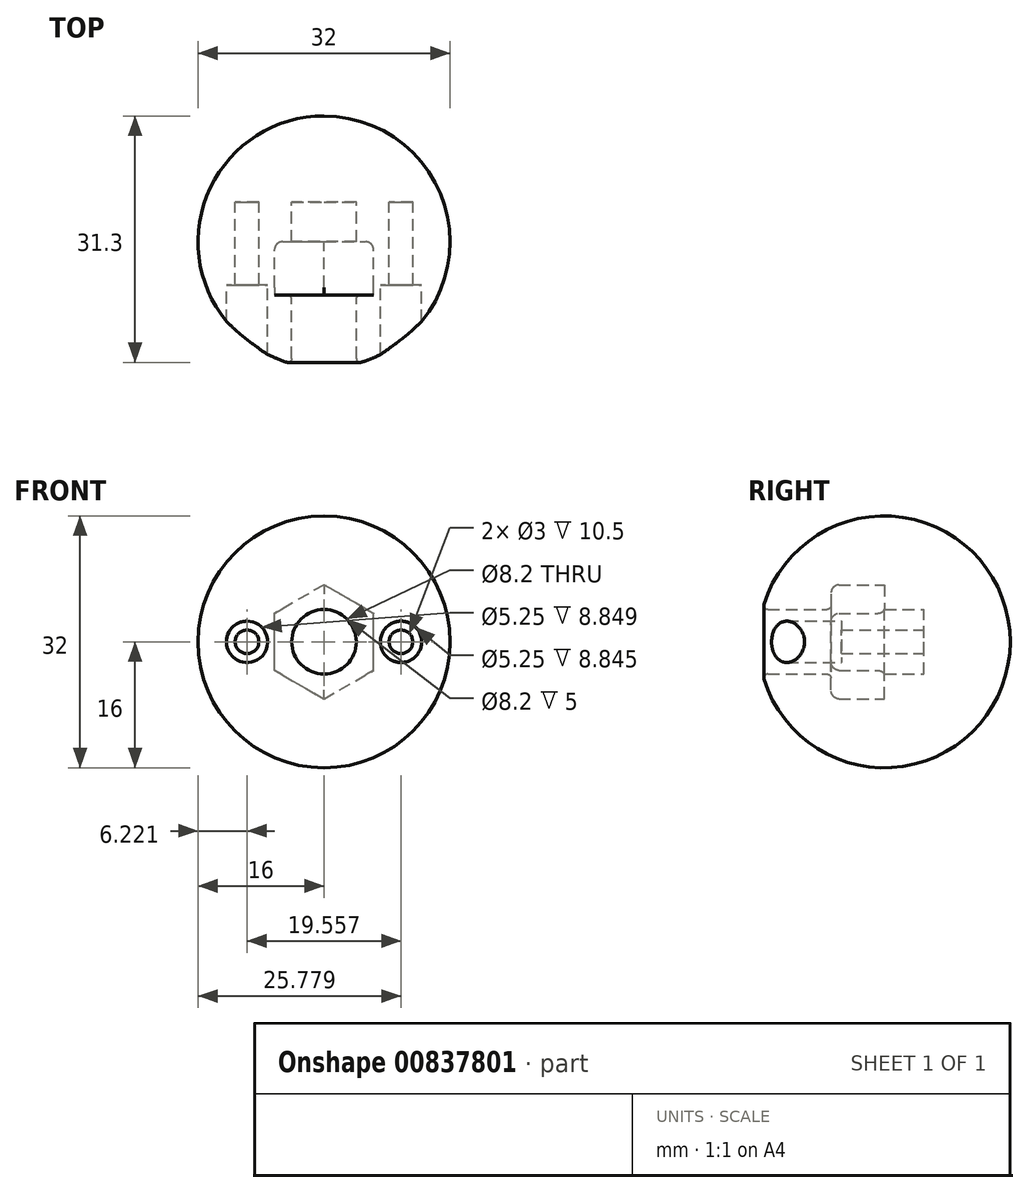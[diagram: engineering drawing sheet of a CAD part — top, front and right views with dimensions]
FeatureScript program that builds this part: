
annotation { "Feature Type Name" : "Feature", "Feature Type Description" : "" }
export const myFeature = defineFeature(function(context is Context, id is Id, definition is map)
    precondition{}
    {
        {
            var Q0;
            Q0=qCreatedBy(makeId("Top.planeOp"),FACE);
            var sketch = newSketch(context, id + "F0", { "sketchPlane" : qUnion([Q0])});
            skArc(sketch, "E0", {"start": v(4.1, -15.47) * mm, "mid": v(0, 16) * mm, "end": v(-4.1, -15.47) * mm});
            skLineSegment(sketch, "E1", {"start": v(0, -15.47) * mm, "end": v(0, 16) * mm});
            skLineSegment(sketch, "E2", {"start": v(0, -12.17) * mm, "end": v(4.1, -12.17) * mm, "construction": true});
            skLineSegment(sketch, "E3", {"start": v(4.1, -12.17) * mm, "end": v(4.1, -15.47) * mm, "construction": true});
            skLineSegment(sketch, "E4", {"start": v(4.1, -15.47) * mm, "end": v(-4.1, -15.47) * mm});
            skPoint(sketch, "E5.orphan", {"position": v(0, -16) * mm});
            skSolve(sketch);
        }
        {
            var Q0;
            {var subQ3=sQuery(id+"F0.wireOp",EDGE,"E1");Q0=makeQuery(id+"F0.imprint","IMPRINT",FACE,{"disambiguationData":[TD([[makeQuery(id+"F0.imprint","IMPRINT",EDGE,{"derivedFrom":subQ3}),-1.0]])]});}
            var Q1;
            Q1=sQuery(id+"F0.wireOp",EDGE,"E1");
            revolve(context, id + "F1", {"surfaceOperationType" : NewSurfaceOperationType.NEW, "entities" : qUnion([Q0]), "axis" : qUnion([Q1]), "revolveType" : RevolveType.FULL});
        }
        {
            var Q0;
            Q0=makeQuery(id+"F1.opRevolve","SWEPT_FACE",FACE,{"disambiguationData":[OSD([sQuery(id+"F0.wireOp",EDGE,"E4")])]});
            extrude(context, id + "F2", {"entities" : qUnion([Q0]), "operationType" : NewBodyOperationType.REMOVE, "oppositeDirection" : true, "depth" : 20.5 * mm, "offsetDistance" : 25 * mm});
        }
        {
            var Q0;
            Q0=makeQuery(id+"F2.boolean.opBoolean","COPY",FACE,{"derivedFrom":makeQuery(id+"F2.opExtrude","CAP_FACE",FACE,{"disambiguationData":[OSD([sQuery(id+"F0.wireOp",EDGE,"E4")])],"isStart":false})});
            var sketch = newSketch(context, id + "F3", { "sketchPlane" : qUnion([Q0])});
            skLineSegment(sketch, "E6", {"start": v(0, 0) * mm, "end": v(-12, 0) * mm, "construction": true});
            skLineSegment(sketch, "E7", {"start": v(0, 0) * mm, "end": v(12, 0) * mm, "construction": true});
            skLineSegment(sketch, "E8", {"start": v(0, 0) * mm, "end": v(0, 7.25) * mm, "construction": true});
            skLineSegment(sketch, "E9", {"start": v(0, 0) * mm, "end": v(0, -7.25) * mm, "construction": true});
            skLineSegment(sketch, "E10", {"start": v(0, 0) * mm, "end": v(3.55, 2.05) * mm, "construction": true});
            skLineSegment(sketch, "E11", {"start": v(0, 0) * mm, "end": v(3.55, -2.05) * mm, "construction": true});
            skLineSegment(sketch, "E12", {"start": v(0, 0) * mm, "end": v(-3.55, -2.05) * mm, "construction": true});
            skLineSegment(sketch, "E13", {"start": v(0, 0) * mm, "end": v(-3.55, 2.05) * mm, "construction": true});
            skLineSegment(sketch, "E14", {"start": v(3.55, 2.05) * mm, "end": v(6.28, 3.63) * mm, "construction": true});
            skLineSegment(sketch, "E15", {"start": v(-3.55, 2.05) * mm, "end": v(-6.28, 3.63) * mm, "construction": true});
            skLineSegment(sketch, "E16", {"start": v(-3.55, -2.05) * mm, "end": v(-6.28, -3.63) * mm, "construction": true});
            skLineSegment(sketch, "E17", {"start": v(3.55, -2.05) * mm, "end": v(6.28, -3.62) * mm, "construction": true});
            skLineSegment(sketch, "E18", {"start": v(0, 7.25) * mm, "end": v(-6.28, 3.62) * mm});
            skLineSegment(sketch, "E19", {"start": v(-6.28, 3.62) * mm, "end": v(-6.28, -3.63) * mm});
            skLineSegment(sketch, "E20", {"start": v(-6.28, -3.63) * mm, "end": v(0, -7.25) * mm});
            skLineSegment(sketch, "E21", {"start": v(0, -7.25) * mm, "end": v(6.28, -3.62) * mm});
            skLineSegment(sketch, "E22", {"start": v(6.28, -3.62) * mm, "end": v(6.28, 3.63) * mm});
            skLineSegment(sketch, "E23", {"start": v(6.28, 3.63) * mm, "end": v(0, 7.25) * mm});
            skLineSegment(sketch, "E24", {"start": v(-6.28, 3.63) * mm, "end": v(-13.28, 3.62) * mm});
            skLineSegment(sketch, "E25", {"start": v(-13.28, 3.62) * mm, "end": v(-13.28, -3.63) * mm});
            skLineSegment(sketch, "E26", {"start": v(-13.28, -3.63) * mm, "end": v(-6.28, -3.63) * mm});
            skLineSegment(sketch, "E27", {"start": v(6.28, 3.63) * mm, "end": v(13.28, 3.63) * mm});
            skLineSegment(sketch, "E28", {"start": v(13.28, 3.63) * mm, "end": v(13.28, -3.62) * mm});
            skLineSegment(sketch, "E29", {"start": v(13.28, -3.62) * mm, "end": v(6.28, -3.62) * mm});
            skCircle(sketch, "E30", {"center": v(-9.78, 0) * mm, "radius": 1.5 * mm});
            skPoint(sketch, "E30.centerSnap0", {"position": v(-9.78, 3.62) * mm});
            skCircle(sketch, "E31", {"center": v(9.78, 0) * mm, "radius": 1.5 * mm});
            skPoint(sketch, "E31.centerSnap0", {"position": v(9.78, 3.63) * mm});
            skSolve(sketch);
        }
        {
            var Q0;
            Q0 = qSketchRegion(id + "F3", true);
            extrude(context, id + "F4", {"entities" : qUnion([Q0]), "operationType" : NewBodyOperationType.ADD, "depth" : 25 * mm, "offsetDistance" : 25 * mm});
        }
        {
            var Q0;
            Q0=makeQuery(id+"F4.opExtrude","CAP_FACE",FACE,{"disambiguationData":[OSD([sQuery(id+"F3.wireOp",EDGE,"E18"),sQuery(id+"F3.wireOp",EDGE,"E20"),sQuery(id+"F3.wireOp",EDGE,"E21"),sQuery(id+"F3.wireOp",EDGE,"E23"),sQuery(id+"F3.wireOp",EDGE,"E24"),sQuery(id+"F3.wireOp",EDGE,"E25"),sQuery(id+"F3.wireOp",EDGE,"E26"),sQuery(id+"F3.wireOp",EDGE,"E27"),sQuery(id+"F3.wireOp",EDGE,"E28"),sQuery(id+"F3.wireOp",EDGE,"E29"),sQuery(id+"F3.wireOp",EDGE,"E30"),sQuery(id+"F3.wireOp",EDGE,"E31")])],"isStart":false});
            var sketch = newSketch(context, id + "F5", { "sketchPlane" : qUnion([Q0])});
            skCircle(sketch, "E32", {"center": v(-9.78, 0) * mm, "radius": 1.5 * mm});
            skCircle(sketch, "E33", {"center": v(9.78, 0) * mm, "radius": 1.5 * mm});
            skSolve(sketch);
        }
        {
            var Q0;
            Q0=makeQuery(id+"F5.imprint","IMPRINT",FACE,{"disambiguationData":[TD([[makeQuery(id+"F5.imprint","IMPRINT",EDGE,{"derivedFrom":sQuery(id+"F5.wireOp",EDGE,"E32")}),-1.0]])]});
            var Q1;
            Q1=makeQuery(id+"F5.imprint","IMPRINT",FACE,{"disambiguationData":[TD([[makeQuery(id+"F5.imprint","IMPRINT",EDGE,{"derivedFrom":sQuery(id+"F5.wireOp",EDGE,"E32")}),1.0]])]});
            var Q2;
            Q2=makeQuery(id+"F5.imprint","IMPRINT",FACE,{"disambiguationData":[TD([[makeQuery(id+"F5.imprint","IMPRINT",EDGE,{"derivedFrom":sQuery(id+"F5.wireOp",EDGE,"E33")}),1.0]])]});
            extrude(context, id + "F6", {"entities" : qUnion([Q0, Q1, Q2]), "operationType" : NewBodyOperationType.REMOVE, "oppositeDirection" : true, "depth" : 25 * mm, "offsetDistance" : 25 * mm});
        }
        {
            var Q0;
            Q0=makeQuery(id+"F3.imprint","IMPRINT",FACE,{"disambiguationData":[TD([[makeQuery(id+"F3.imprint","IMPRINT",EDGE,{"derivedFrom":sQuery(id+"F3.wireOp",EDGE,"E18")}),1.0]])]});
            var Q1;
            Q1=makeQuery(id+"F3.imprint","IMPRINT",FACE,{"disambiguationData":[TD([[makeQuery(id+"F3.imprint","IMPRINT",EDGE,{"derivedFrom":sQuery(id+"F3.wireOp",EDGE,"E19")}),-1.0]])]});
            var Q2;
            Q2=makeQuery(id+"F3.imprint","IMPRINT",FACE,{"disambiguationData":[TD([[makeQuery(id+"F3.imprint","IMPRINT",EDGE,{"derivedFrom":sQuery(id+"F3.wireOp",EDGE,"E22")}),-1.0]])]});
            extrude(context, id + "F7", {"entities" : qUnion([Q0, Q1, Q2]), "operationType" : NewBodyOperationType.ADD, "depth" : 5 * mm, "offsetDistance" : 25 * mm});
        }
        {
            var Q0;
            Q0=qCreatedBy(makeId("Top.planeOp"),FACE);
            var sketch = newSketch(context, id + "F8", { "sketchPlane" : qUnion([Q0])});
            skCircle(sketch, "E34", {"center": v(0, 0) * mm, "radius": 16 * mm});
            skLineSegment(sketch, "E35.bottom", {"start": v(22.52, -32.43) * mm, "end": v(-22.52, -32.43) * mm});
            skLineSegment(sketch, "E35.top", {"start": v(22.52, 32.43) * mm, "end": v(-22.52, 32.43) * mm});
            skLineSegment(sketch, "E35.left", {"start": v(22.52, -32.43) * mm, "end": v(22.52, 32.43) * mm});
            skLineSegment(sketch, "E35.right", {"start": v(-22.52, -32.43) * mm, "end": v(-22.52, 32.43) * mm});
            skLineSegment(sketch, "E36", {"start": v(0, 0) * mm, "end": v(0, -16) * mm});
            skLineSegment(sketch, "E37", {"start": v(0, -16) * mm, "end": v(0, 16) * mm});
            skLineSegment(sketch, "E38", {"start": v(0, -32.43) * mm, "end": v(0, 32.43) * mm});
            skSolve(sketch);
        }
        {
            var Q0;
            Q0=makeQuery(id+"F7.opExtrude","CAP_FACE",FACE,{"disambiguationData":[OSD([sQuery(id+"F0.wireOp",EDGE,"E0"),sQuery(id+"F0.wireOp",EDGE,"E4"),sQuery(id+"F3.wireOp",EDGE,"E18"),sQuery(id+"F3.wireOp",EDGE,"E20"),sQuery(id+"F3.wireOp",EDGE,"E21"),sQuery(id+"F3.wireOp",EDGE,"E23"),sQuery(id+"F3.wireOp",EDGE,"E24"),sQuery(id+"F3.wireOp",EDGE,"E25"),sQuery(id+"F3.wireOp",EDGE,"E26"),sQuery(id+"F3.wireOp",EDGE,"E27"),sQuery(id+"F3.wireOp",EDGE,"E28"),sQuery(id+"F3.wireOp",EDGE,"E29"),sQuery(id+"F3.wireOp",EDGE,"E30"),sQuery(id+"F3.wireOp",EDGE,"E31")])],"isStart":false});
            extrude(context, id + "F9", {"entities" : qUnion([Q0]), "depth" : 25 * mm, "offsetDistance" : 25 * mm});
        }
        {
            var Q0;
            {var subQ0=sQuery(id+"F8.wireOp",EDGE,"E35.left");Q0=makeQuery(id+"F8.imprint","IMPRINT",FACE,{"disambiguationData":[TD([[makeQuery(id+"F8.imprint","IMPRINT",EDGE,{"derivedFrom":subQ0}),1.0]])]});}
            var Q1;
            Q1=sQuery(id+"F8.wireOp",EDGE,"E38");
            revolve(context, id + "F10", {"operationType" : NewBodyOperationType.REMOVE, "surfaceOperationType" : NewSurfaceOperationType.NEW, "entities" : qUnion([Q0]), "axis" : qUnion([Q1]), "revolveType" : RevolveType.FULL, "oppositeDirection" : true});
        }
        {
            var Q0;
            Q0=makeQuery(id+"F9.opExtrude","CAP_FACE",FACE,{"disambiguationData":[OSD([sQuery(id+"F0.wireOp",EDGE,"E0"),sQuery(id+"F0.wireOp",EDGE,"E4"),sQuery(id+"F3.wireOp",EDGE,"E18"),sQuery(id+"F3.wireOp",EDGE,"E20"),sQuery(id+"F3.wireOp",EDGE,"E21"),sQuery(id+"F3.wireOp",EDGE,"E23"),sQuery(id+"F3.wireOp",EDGE,"E24"),sQuery(id+"F3.wireOp",EDGE,"E25"),sQuery(id+"F3.wireOp",EDGE,"E26"),sQuery(id+"F3.wireOp",EDGE,"E27"),sQuery(id+"F3.wireOp",EDGE,"E28"),sQuery(id+"F3.wireOp",EDGE,"E29"),sQuery(id+"F3.wireOp",EDGE,"E30"),sQuery(id+"F3.wireOp",EDGE,"E31")])],"isStart":true});
            var sketch = newSketch(context, id + "F11", { "sketchPlane" : qUnion([Q0])});
            skCircle(sketch, "E39", {"center": v(-9.78, 0) * mm, "radius": 2.62 * mm});
            skCircle(sketch, "E40", {"center": v(9.78, 0) * mm, "radius": 2.62 * mm});
            skLineSegment(sketch, "E41", {"start": v(-6.28, -3.62) * mm, "end": v(-6.28, 3.63) * mm});
            skLineSegment(sketch, "E42", {"start": v(6.28, -3.63) * mm, "end": v(6.28, 3.62) * mm});
            skSolve(sketch);
        }
        {
            var Q0;
            Q0=makeQuery(id+"F11.imprint","IMPRINT",FACE,{"disambiguationData":[TD([[makeQuery(id+"F11.imprint","IMPRINT",EDGE,{"derivedFrom":sQuery(id+"F11.wireOp",EDGE,"E39")}),1.0]])]});
            var Q1;
            Q1=makeQuery(id+"F11.imprint","IMPRINT",FACE,{"disambiguationData":[TD([[makeQuery(id+"F11.imprint","IMPRINT",EDGE,{"derivedFrom":sQuery(id+"F11.wireOp",EDGE,"E40")}),1.0]])]});
            extrude(context, id + "F12", {"entities" : qUnion([Q0, Q1]), "operationType" : NewBodyOperationType.REMOVE, "oppositeDirection" : true, "depth" : 25 * mm, "offsetDistance" : 25 * mm});
        }
        {
            var Q0;
            Q0=makeQuery(id+"F11.imprint","IMPRINT",FACE,{"disambiguationData":[TD([[makeQuery(id+"F11.imprint","IMPRINT",EDGE,{"derivedFrom":sQuery(id+"F11.wireOp",EDGE,"E39")}),1.0]])]});
            var Q1;
            Q1=makeQuery(id+"F11.imprint","IMPRINT",FACE,{"disambiguationData":[TD([[makeQuery(id+"F11.imprint","IMPRINT",EDGE,{"derivedFrom":sQuery(id+"F11.wireOp",EDGE,"E40")}),1.0]])]});
            extrude(context, id + "F13", {"entities" : qUnion([Q0, Q1]), "operationType" : NewBodyOperationType.ADD, "oppositeDirection" : true, "depth" : 5.5 * mm, "offsetDistance" : 25 * mm});
        }
        {
            var Q0;
            Q0=makeQuery(id+"F10.boolean.opBoolean","INTERSECT",EDGE,{"derivedFrom":[makeQuery(id+"F9.opExtrude","SWEPT_FACE",FACE,{"disambiguationData":[OSD([sQuery(id+"F0.wireOp",EDGE,"E0"),sQuery(id+"F0.wireOp",EDGE,"E4")])]}),makeQuery(id+"F10.opRevolve","SWEPT_FACE",FACE,{"disambiguationData":[OSD([sQuery(id+"F8.wireOp",EDGE,"E34")])]})]});
            fillet(context, id + "F14", {"entities" : qUnion([Q0]), "radius" : .5 * mm, "tangentPropagation" : true, "allowEdgeOverflow" : false});
        }
        {
            var Q0;
            Q0=makeQuery(id+"F11.imprint","IMPRINT",FACE,{"disambiguationData":[TD([[makeQuery(id+"F11.imprint","IMPRINT",EDGE,{"derivedFrom":sQuery(id+"F11.wireOp",EDGE,"E41")}),-1.0]])]});
            extrude(context, id + "F15", {"entities" : qUnion([Q0]), "operationType" : NewBodyOperationType.REMOVE, "oppositeDirection" : true, "depth" : 6.8 * mm, "offsetDistance" : 25 * mm});
        }
        {
            var Q0;
            Q0=makeQuery(id+"F9.opExtrude","CAP_EDGE",EDGE,{"disambiguationData":[OSD([sQuery(id+"F3.wireOp",EDGE,"E28")])],"isStart":true});
            var Q1;
            Q1=makeQuery(id+"F9.opExtrude","CAP_EDGE",EDGE,{"disambiguationData":[OSD([sQuery(id+"F3.wireOp",EDGE,"E29")])],"isStart":true});
            var Q2;
            Q2=makeQuery(id+"F15.boolean.opBoolean","COPY",EDGE,{"derivedFrom":makeQuery(id+"F15.opExtrude","CAP_EDGE",EDGE,{"disambiguationData":[OSD([sQuery(id+"F11.wireOp",EDGE,"E41")])],"isStart":true})});
            var Q3;
            Q3=makeQuery(id+"F9.opExtrude","CAP_EDGE",EDGE,{"disambiguationData":[OSD([sQuery(id+"F3.wireOp",EDGE,"E27")])],"isStart":true});
            var Q4;
            Q4=makeQuery(id+"F15.boolean.opBoolean","COPY",EDGE,{"derivedFrom":makeQuery(id+"F15.opExtrude","CAP_EDGE",EDGE,{"disambiguationData":[OSD([sQuery(id+"F11.wireOp",EDGE,"E42")])],"isStart":true})});
            var Q5;
            Q5=makeQuery(id+"F9.opExtrude","CAP_EDGE",EDGE,{"disambiguationData":[OSD([sQuery(id+"F3.wireOp",EDGE,"E24")])],"isStart":true});
            var Q6;
            Q6=makeQuery(id+"F9.opExtrude","CAP_EDGE",EDGE,{"disambiguationData":[OSD([sQuery(id+"F3.wireOp",EDGE,"E25")])],"isStart":true});
            var Q7;
            Q7=makeQuery(id+"F9.opExtrude","CAP_EDGE",EDGE,{"disambiguationData":[OSD([sQuery(id+"F3.wireOp",EDGE,"E26")])],"isStart":true});
            var Q8;
            Q8=makeQuery(id+"F15.boolean.opBoolean","COPY",EDGE,{"derivedFrom":makeQuery(id+"F15.opExtrude","CAP_EDGE",EDGE,{"disambiguationData":[OSD([sQuery(id+"F3.wireOp",EDGE,"E18")])],"isStart":false})});
            var Q9;
            Q9=makeQuery(id+"F15.boolean.opBoolean","COPY",EDGE,{"derivedFrom":makeQuery(id+"F15.opExtrude","CAP_EDGE",EDGE,{"disambiguationData":[OSD([sQuery(id+"F3.wireOp",EDGE,"E21")])],"isStart":false})});
            var Q10;
            Q10=makeQuery(id+"F15.boolean.opBoolean","COPY",EDGE,{"derivedFrom":makeQuery(id+"F15.opExtrude","CAP_EDGE",EDGE,{"disambiguationData":[OSD([sQuery(id+"F3.wireOp",EDGE,"E20")])],"isStart":false})});
            var Q11;
            Q11=makeQuery(id+"F15.boolean.opBoolean","COPY",EDGE,{"derivedFrom":makeQuery(id+"F15.opExtrude","CAP_EDGE",EDGE,{"disambiguationData":[OSD([sQuery(id+"F3.wireOp",EDGE,"E23")])],"isStart":false})});
            fillet(context, id + "F16", {"entities" : qUnion([Q0, Q1, Q2, Q3, Q4, Q5, Q6, Q7, Q8, Q9, Q10, Q11]), "radius" : 1 * mm, "tangentPropagation" : true, "allowEdgeOverflow" : false});
        }
        {
            var Q0;
            Q0=makeQuery(id+"F15.boolean.opBoolean","COPY",EDGE,{"derivedFrom":makeQuery(id+"F15.opExtrude","CAP_EDGE",EDGE,{"disambiguationData":[OSD([sQuery(id+"F0.wireOp",EDGE,"E0"),sQuery(id+"F0.wireOp",EDGE,"E4")])],"isStart":false})});
            fillet(context, id + "F17", {"entities" : qUnion([Q0]), "radius" : .5 * mm, "tangentPropagation" : true, "allowEdgeOverflow" : false});
        }
    });
